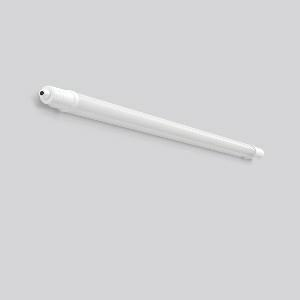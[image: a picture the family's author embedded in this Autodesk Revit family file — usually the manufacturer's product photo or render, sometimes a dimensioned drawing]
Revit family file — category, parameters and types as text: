
# Revit family: hb_702_451217_002_455f
name_source: partatom
category: Lighting Fixtures
units: mm (PartAtom-declared; Revit-internal decimal feet)

## family parameters
Cut with Voids When Loaded = No
Host = Face
Light Source = No
Part Type = Normal
Room Calculation Point = No
Round Connector Dimension = Use Diameter
Shared = No

## types (1)
- MultiLumen 1 (1 x LED Modul 840, 6000 lm, 4000)
    Apparent Load = 52 VA
    CIE Flux Codes = 35 63 84 79 100
    Color Rendering = 80
    Color Temperature = 4000
    Default Elevation = 1800 mm
    Description = Series: HB 702
Moisture-proof luminaire. Side panels: plastic, white polycarbonate. Diffuser: plastic (polycarbonate), opal. Symmetrical light distribution. Homogeneous light distribution. Ceiling mounting stainless steel brackets and triangular brackets for pendant mounting included in delivery. Converter encapsulated, integrated and permanently connected to the diffuser and side panel. Cable screw fittings for convenient wiring. Turn lock fastener on both sides for easy installation. Luminaire with integrated 3-phase through-wiring to connect multiple luminaires. MultiLumen: 2 steps adjustable luminous flux. Factory setting is the highest luminous flux. Luminaire with limited surface temperature in accordance with EN 60598-2-24 for use in environments in which a deposit of conductive dust on the luminaire can be expected. 
Colour: white
Length: 1560 mm
Width: 53 mm
Height: 53 mm
Lamp: LED
Socket: without socket
Colour temperature: 4000K
Colour rendering index (CRI): 80
System power: 52 W
Rated luminous flux: 6000 lm
Luminous efficiency: 115 lm/W
System power 2: 35 W
Rated luminous flux 2: 4000 lm
Luminous efficiency 2: 114 lm/W
Control gear: Regulated power supply
Protection class: II
Type of protection: IP 65
    Height = 53 mm
    Lamp = 1 x LED Modul 840
    Lamp Light Flux = 6000 lm
    Lamp count = 1
    Length = 1560 mm
    Lifetime = 50000 h
    Luminous efficacy = 115 lm/W
    Manufacturer = RZB
    ModVariant = No
    Model = 451217.002
    Mounting Place = Wall, Ceiling
    Mounting Type = Surface mounted
    Number of Poles = 1
    OnlyDefault = Yes
    Power Factor = 1
    Product Name = HB 702
    Product group = Surface mounted luminaires for moist/humid enviroments
    ProductGroupID = 308
    Protection Class = Protection class II
    Protection Degree = IP 65
    RLX_Detail_Level = 1
    RLX_Emergency_Light_Flux = 0 lm
    RLX_Emergency_Type = 0
    RLX_Emergency_Type_DB = No
    RlxData = <blob elided: 57369 chars, md5=00017e5d>
    Socket = socket
    Standby Power = 0 W
    System Light Flux = 6000 lm
    System Power = 52 W
    Type Comments = MultiLumen 1
    Type Image = 451217.002.jpg
    URL = http://relux.com
    VarID = multilumen_1
    Voltage = 230 V
    Voltage Range = 220-240 V
    Weight = 0.00 kg
    Width = 53 mm

## geometry (parser evidence)
native form markers: Blend x4, Sweep x13
no freeform markers — native parametric forms only
